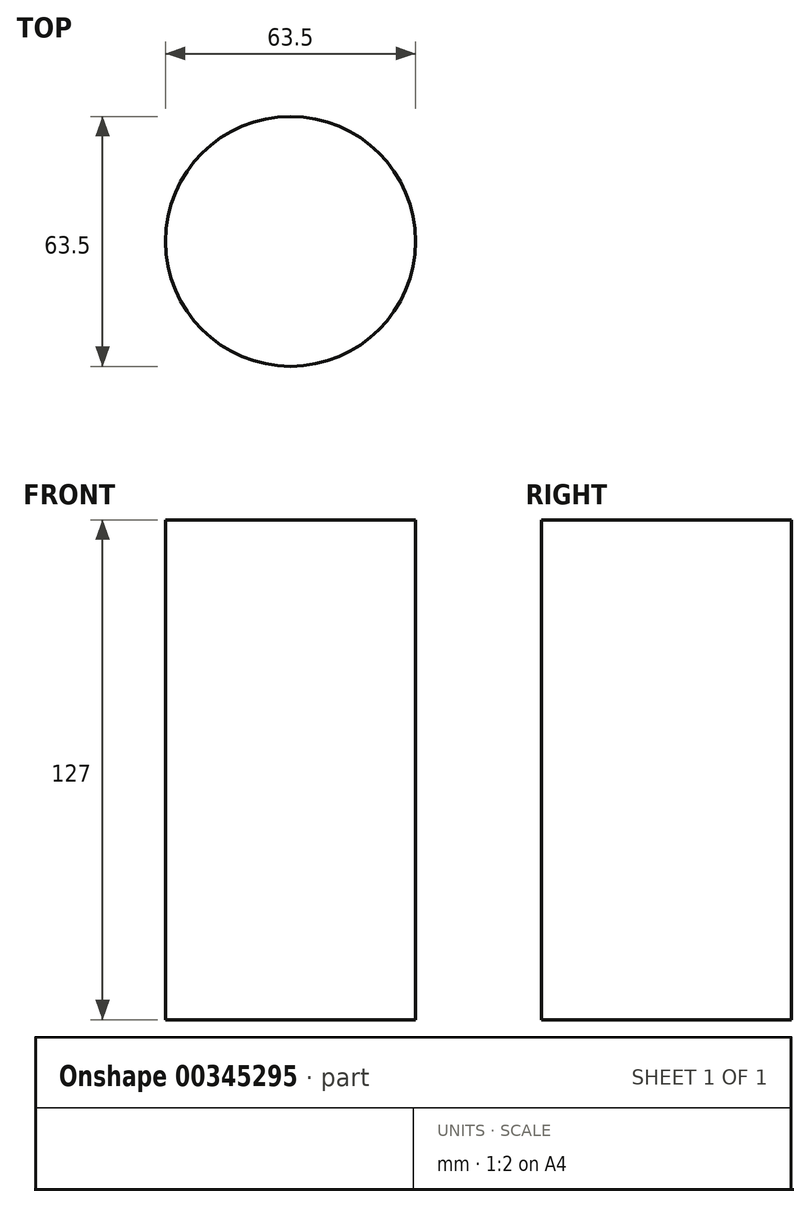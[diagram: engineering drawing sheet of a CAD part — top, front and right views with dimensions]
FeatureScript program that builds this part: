
annotation { "Feature Type Name" : "Feature", "Feature Type Description" : "" }
export const myFeature = defineFeature(function(context is Context, id is Id, definition is map)
    precondition{}
    {
        {
            var Q0;
            Q0=qCreatedBy(makeId("Top.planeOp"),FACE);
            var sketch = newSketch(context, id + "F0", { "sketchPlane" : qUnion([Q0])});
            skCircle(sketch, "E0", {"center": v(0, 0) * mm, "radius": 31.75 * mm});
            skSolve(sketch);
        }
        {
            var Q0;
            Q0 = qSketchRegion(id + "F0", true);
            extrude(context, id + "F1", {"entities" : qUnion([Q0]), "depth" : 127 * mm});
        }
    });
